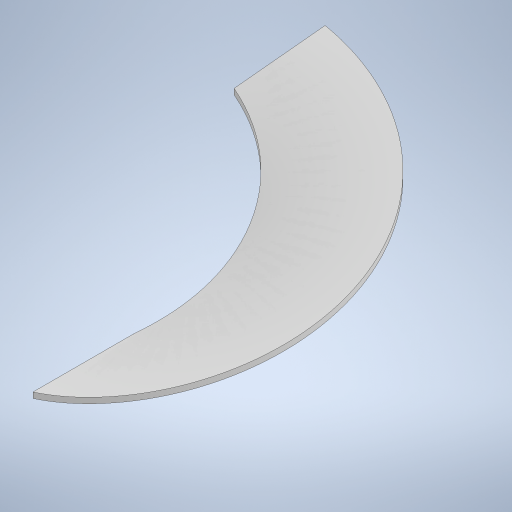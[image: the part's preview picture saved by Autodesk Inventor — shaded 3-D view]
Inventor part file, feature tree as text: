
AUTODESK INVENTOR PART (.ipt)
format: ipt  version: 2024 (Build 280153000, 153)  size: 253,952 bytes
history: native  units: mm
features: sketch x3, plane x1, helix x1
ambient origin geometry x8: Origin, YZ Plane, XZ Plane, XY Plane, X Axis, Y Axis, Z Axis, Center Point
bodies: Solid1 (feature_tree)
feature tree (5):
  sketch  "Sketch1"  dims[d1=3.2mm]
  plane  "Work Plane1"
  sketch  "Sketch2"  dims[d2=175.0mm]
  helix  "Coil1"  [1 undecoded]
  sketch  "Sketch3"  dims[d3=175.0mm d4=175.0mm d5=10.0mm d6=5.142857mm d7=0.0mm d8=90.0deg d9=90.0deg d10=0.0mm d11=0.0mm d12=30.15mm d13=87.5mm d14=3.2mm]
note: 1 required parameter value undecoded (feature->parameter linkage not recoverable at this tier; creation-order binding heuristic only, values carry confidence <= 0.55)
